# Revit family: Indirect-Water-Heater_AO_Smith-IT-600_B_B
name_source: partatom
category: Mechanical Equipment
revit_build: Autodesk Revit 2016 (Build: 20170117_1200(x64)
units: mm (PartAtom-declared; Revit-internal decimal feet)

## family parameters
Always vertical = Yes
Cut with Voids When Loaded = No
OmniClass Number = 23.75.00.00
OmniClass Title = Climate Control (HVAC)
Part Type = Normal
Room Calculation Point = No
Round Connector Dimension = Use Radius
Shared = No
Work Plane-Based = No

## types (1)
- IT 600 B B
    1e Maintenance (check-up) = 3 maanden na installatie
    2nd Maintenance (general maintenance) = 12 maanden na installatie
    Assembly Code = D3010
    BIM Content Developer = CAD & Company
    BIM Content Developer URL = http://www.cadcompany.be
    Category = Mechanical Equipment
    Cold Water Connection R = 1 1/2"
    Description = Indirecte Boiler met 1 warmtewisselaar
    Destination / Counrty = België
    Diameter (with insulation) = 910 mm  [stored 2.98556 ft]
    Diameter (without insulation) = 750 mm  [stored 2.46063 ft]
    Draw-off Capacity @ ΔT = 28°C after 120 min. = 7515.0 L
    Draw-off Capacity @ ΔT = 28°C after 30 min. = 2723.0 L
    Draw-off Capacity @ ΔT = 28°C after 60 min. = 4321.0 L
    Draw-off Capacity @ ΔT = 28°C after 90 min. = 5918.0 L
    Draw-off Capacity @ ΔT = 44°C after 120 min. = 4782.0 L
    Draw-off Capacity @ ΔT = 44°C after 30 min. = 1733.0 L
    Draw-off Capacity @ ΔT = 44°C after 60 min. = 2749.0 L
    Draw-off Capacity @ ΔT = 44°C after 90 min. = 3766.0 L
    Draw-off Capacity @ ΔT = 50°C after 120 min. = 4208.0 L
    Draw-off Capacity @ ΔT = 50°C after 30 min. = 1525.0 L
    Draw-off Capacity @ ΔT = 50°C after 60 min. = 2420.0 L
    Draw-off Capacity @ ΔT = 50°C after 90 min. = 3314.0 L
    Draw-off Capacity @ ΔT = 55°C after 120 min. = 3826.0 L
    Draw-off Capacity @ ΔT = 55°C after 30 min. = 1386.0 L
    Draw-off Capacity @ ΔT = 55°C after 60 min. = 2200.0 L
    Draw-off Capacity @ ΔT = 55°C after 90 min. = 3013.0 L
    Draw-off Capacity @ ΔT = 70°C after 120 min. = 3006.0 L
    Draw-off Capacity @ ΔT = 70°C after 30 min. = 1089.0 L
    Draw-off Capacity @ ΔT = 70°C after 60 min. = 1728.0 L
    Draw-off Capacity @ ΔT = 70°C after 90 min. = 2367.0 L
    Empty Weight = 241.00 kg
    Flow Rate - Volume L/h = 4472
    Heating Up Time @ ΔT = 28°C = 12
    Heating Up Time @ ΔT = 44°C = 19
    Heating Up Time @ ΔT = 50°C = 22
    Heating Up Time @ ΔT = 55°C = 24
    Heating Up Time @ ΔT = 70°C = 30
    Height (with insulation) = 1840 mm  [stored 6.03675 ft]
    Height (without insulation) = 1805 mm  [stored 5.92192 ft]
    Height Cold Water Inlet = 85 mm  [stored 0.278871 ft]
    Height Warm Water Outlet = 1805 mm  [stored 5.92192 ft]
    Host = Unhosted
    Hot / Warm Water Connection R = 1 1/2"
    Insulation Thickness = 80 mm  [stored 0.262467 ft]
    Maintenance Interval = 12 maanden
    Manufacturer = A.O. Smith Water Products Company b.v.
    Manufacturer Number = E 7110
E 7110
E 7110
    Max. Operating Pressure - bottom heat exchanger = 1600000.0 Pa
    Max. Operating Pressure - tank = 1000000.0 Pa
    Max. Tempature - bottom heat exchanger = 110 °C
    Max. Temperature - tank = 95 °C
    Model = IT 600 B B
    NLSfB = 51.11
    Nominal Output - bottom heat exchanger = 104000 W
    Operating Weight = 884.00 kg
    Packaging Height = 1930 mm  [stored 6.33202 ft]
    Packaging Length = 870 mm  [stored 2.85433 ft]
    Packaging Width = 870 mm  [stored 2.85433 ft]
    Pressure Loss - bottom heat exchanger 80ºC/60ºC = 104000.0 Pa
    Product Documentation Link = https://www.aosmithinternational.com
    Product Instruction Link = https://www.aosmithinternational.com
    Productcode = 8717449180225
    Productversion = 1.0
    Recovery Rate @ ΔT = 28°C (ltr/hr) = 3194
    Recovery Rate @ ΔT = 44°C (ltr/hr) = 2033
    Recovery Rate @ ΔT = 50°C (ltr/hr) = 1789
    Recovery Rate @ ΔT = 55°C (ltr/hr) = 1626
    Recovery Rate @ ΔT = 70°C (ltr/hr) = 1278
    Serial Number = 8717449180225
    Stand-by Loss = 0 W
    Stand-by Loss - daily (Watt/24H) = 0
    Storage Capacity - bottom heat exchanger = 29.3 m³
    Storage Capacity - tank = 643 m³
    Surface bottom heat Exchanger = 3.45 m²
    T&P Connection Rp = 1"
    Transport Weight = 251.00 kg
    Type of Packaging = Plastic en Hout
    URL = www.aosmith.be
    Warranty on Parts = 12 maanden
    Warranty on Tank = 36 maanden
    Workspace Diameter = 1910 mm  [stored 6.2664 ft]
    Workspace Height = 1910 mm  [stored 6.2664 ft]

note: [stored X ft] marks values corroborated as IEEE doubles in the binary element streams (Revit-internal decimal feet)

## geometry (parser evidence)
native form markers: Blend x2, Sweep x20
no freeform markers — native parametric forms only
